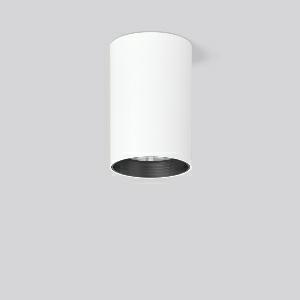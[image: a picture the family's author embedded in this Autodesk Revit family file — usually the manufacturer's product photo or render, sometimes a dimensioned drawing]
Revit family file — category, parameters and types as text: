
# Revit family: heledon_maxi_a_931228_002_3_ef34
name_source: partatom
category: Lighting Fixtures
units: mm (PartAtom-declared; Revit-internal decimal feet)

## family parameters
Cut with Voids When Loaded = No
Host = Face
Light Source = No
Part Type = Normal
Room Calculation Point = No
Round Connector Dimension = Use Diameter
Shared = No

## types (1)
- HELEDON maxi A (1 x LED Modul 935, 3600 lm, 3500)
    Apparent Load = 35 VA
    Approval mark = CE
    CIE Flux Codes = 96 100 100 100 100
    Color Rendering = 92
    Color Temperature = 3500
    Default Elevation = 1800 mm
    Description = Series: HELEDON maxi
Cylindrical surface-mounted downlight. Housing: die-cast aluminium, powder-coated. Internal ceiling frame polycarbonate with bayonet mounting. Black plastic ring and recessed LED to prevent glare from the side. Optical assembly with lens made of plastic (polycarbonate) for the best homogeneous light distribution - can be changed without tools. Best colour rendering index Ra>90. Suitable for Ceiling mounting. Easy installation with a separate ceiling frame with bayonet mounting and plug connection. Driver integrated. Connected via plug-in connector. High quality converter without flickering and stroboscopic effect. The following accessories can be mounted without use of tools: interchangeable lenses, decorative glasses, honeycomb louvre, clear and frosted diffusers, white interchangeable plastic ring. 
Colour: traffic white, matt (RAL 9016)
Diameter: 123 mm
Height: 183 mm
Lamp: LED
Socket: without socket
Colour temperature: 3500K
Colour rendering index (CRI): 92
System power: 35 W
Rated luminous flux: 3600 lm
Luminous efficiency: 103 lm/W
Control gear: Regulated power supply
Protection class: I
Type of protection: IP 20
    Height = 183 mm
    Lamp = 1 x LED Modul 935
    Lamp Light Flux = 3600 lm
    Lamp count = 1
    Length = 123 mm
    Lifetime = 50000 h
    Luminous efficacy = 103 lm/W
    Manufacturer = RZB
    ModVariant = No
    Model = 931228.002.3
    Mounting Place = Ceiling
    Mounting Type = Surface mounted
    Number of Poles = 1
    OnlyDefault = Yes
    Power Factor = 1
    Product Name = HELEDON maxi A
    Product group = Surface mounted downlights
    ProductGroupID = 302
    Protection Class = Protection class I
    Protection Degree = IP 20
    RLX_Detail_Level = 1
    RLX_Emergency_Light_Flux = 0 lm
    RLX_Emergency_Type = 0
    RLX_Emergency_Type_DB = No
    RlxData = <blob elided: 98081 chars, md5=69393a75>
    Socket = socket
    Standby Power = 0 W
    System Light Flux = 3600 lm
    System Power = 35 W
    Type Comments = Product without accessories
    Type Image = 931193.002.jpg
    URL = http://relux.com
    VarID = ---
    Voltage = 230 V
    Voltage Range = 220-240 V
    Weight = 0.00 kg
    Width = 0 mm  [stored 0 ft]

note: [stored X ft] marks values corroborated as IEEE doubles in the binary element streams (Revit-internal decimal feet)

## geometry (parser evidence)
native form markers: Blend x4, Sweep x9
no freeform markers — native parametric forms only
